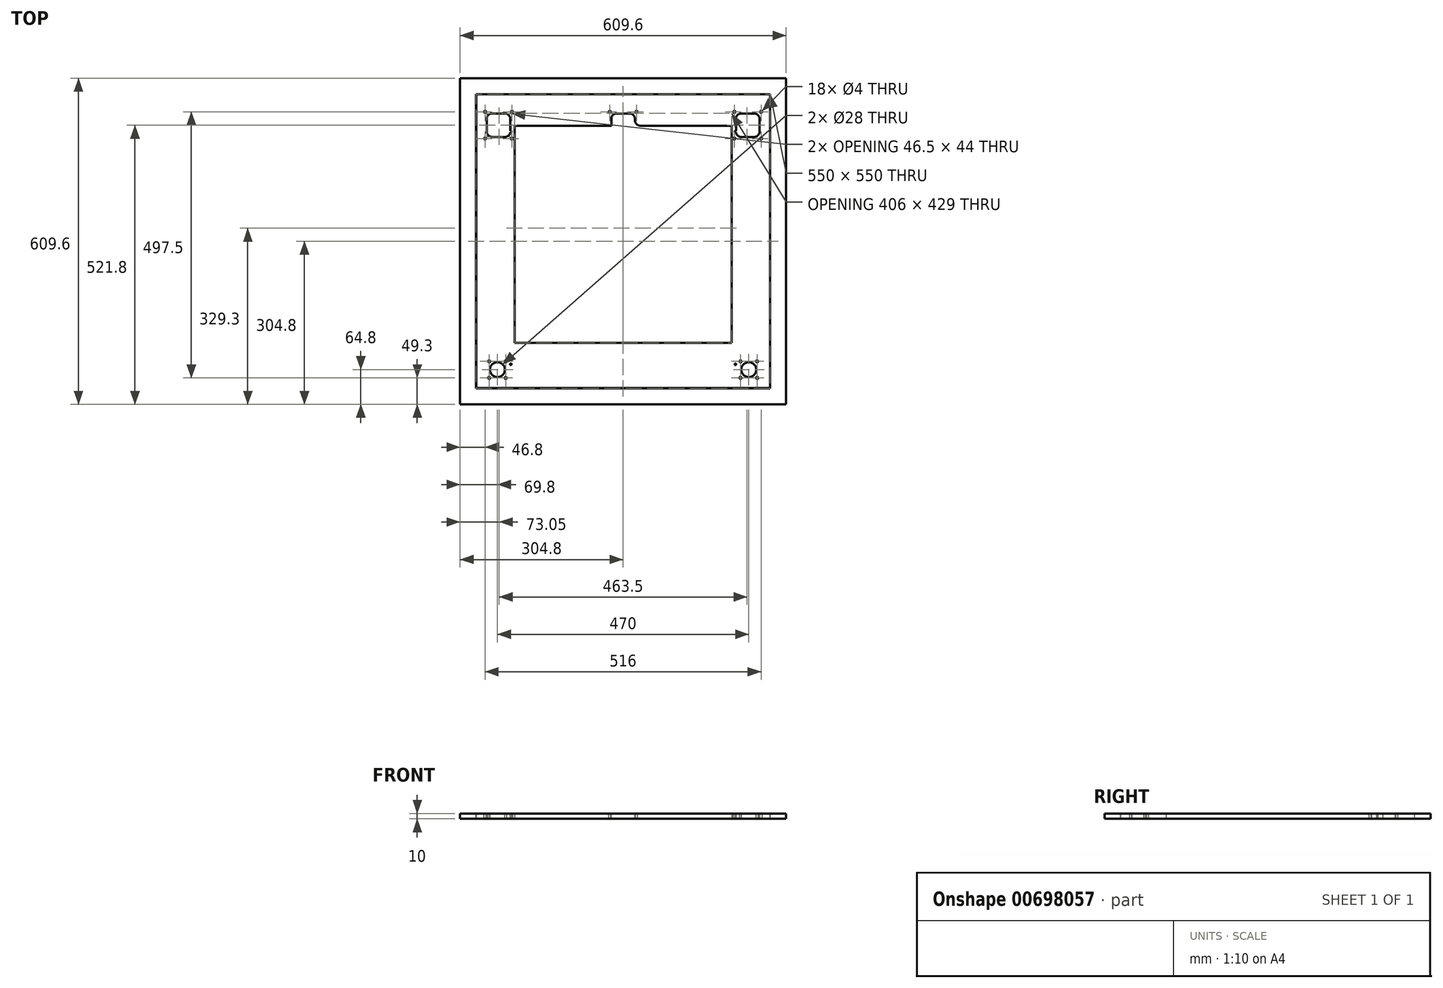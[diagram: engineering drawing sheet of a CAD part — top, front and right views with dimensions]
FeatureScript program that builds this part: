
annotation { "Feature Type Name" : "Feature", "Feature Type Description" : "" }
export const myFeature = defineFeature(function(context is Context, id is Id, definition is map)
    precondition{}
    {
        {
            var Q0;
            Q0=qCreatedBy(makeId("Top.planeOp"),FACE);
            var sketch = newSketch(context, id + "F0", { "sketchPlane" : qUnion([Q0])});
            skPoint(sketch, "E0.middle", {"position": v(0, 0) * mm});
            skLineSegment(sketch, "E1.bottom", {"start": v(-203, -190) * mm, "end": v(203, -190) * mm});
            skLineSegment(sketch, "E1.top", {"start": v(-203, 216) * mm, "end": v(203, 216) * mm});
            skLineSegment(sketch, "E1.left", {"start": v(-203, -190) * mm, "end": v(-203, 216) * mm});
            skLineSegment(sketch, "E1.right", {"start": v(203, -190) * mm, "end": v(203, 216) * mm});
            skLineSegment(sketch, "E2.bottom", {"start": v(274.64, -274.64) * mm, "end": v(-274.64, -274.64) * mm});
            skLineSegment(sketch, "E2.top", {"start": v(274.64, 274.64) * mm, "end": v(-274.64, 274.64) * mm});
            skLineSegment(sketch, "E2.left", {"start": v(274.64, -274.64) * mm, "end": v(274.64, 274.64) * mm});
            skLineSegment(sketch, "E2.right", {"start": v(-274.64, -274.64) * mm, "end": v(-274.64, 274.64) * mm});
            skLineSegment(sketch, "E3.bottom", {"start": v(-274.64, 274.64) * mm, "end": v(-223.84, 274.64) * mm});
            skLineSegment(sketch, "E3.top", {"start": v(-274.64, 223.84) * mm, "end": v(-223.84, 223.84) * mm});
            skLineSegment(sketch, "E3.left", {"start": v(-274.64, 274.64) * mm, "end": v(-274.64, 223.84) * mm});
            skLineSegment(sketch, "E3.right", {"start": v(-223.84, 274.64) * mm, "end": v(-223.84, 223.84) * mm});
            skLineSegment(sketch, "E4.bottom", {"start": v(274.64, 274.64) * mm, "end": v(223.84, 274.64) * mm});
            skLineSegment(sketch, "E4.top", {"start": v(274.64, 223.84) * mm, "end": v(223.84, 223.84) * mm});
            skLineSegment(sketch, "E4.left", {"start": v(274.64, 274.64) * mm, "end": v(274.64, 223.84) * mm});
            skLineSegment(sketch, "E4.right", {"start": v(223.84, 274.64) * mm, "end": v(223.84, 223.84) * mm});
            skLineSegment(sketch, "E5.bottom", {"start": v(-274.64, -274.64) * mm, "end": v(-223.84, -274.64) * mm});
            skLineSegment(sketch, "E5.top", {"start": v(-274.64, -223.84) * mm, "end": v(-223.84, -223.84) * mm});
            skLineSegment(sketch, "E5.left", {"start": v(-274.64, -274.64) * mm, "end": v(-274.64, -223.84) * mm});
            skLineSegment(sketch, "E5.right", {"start": v(-223.84, -274.64) * mm, "end": v(-223.84, -223.84) * mm});
            skLineSegment(sketch, "E6.bottom", {"start": v(274.64, -274.64) * mm, "end": v(223.84, -274.64) * mm});
            skLineSegment(sketch, "E6.top", {"start": v(274.64, -223.84) * mm, "end": v(223.84, -223.84) * mm});
            skLineSegment(sketch, "E6.left", {"start": v(274.64, -274.64) * mm, "end": v(274.64, -223.84) * mm});
            skLineSegment(sketch, "E6.right", {"start": v(223.84, -274.64) * mm, "end": v(223.84, -223.84) * mm});
            skSolve(sketch);
        }
        {
            var Q0;
            Q0 = qSketchRegion(id + "F0", true);
            var Q1;
            {var subQ5=sQuery(id+"F0.wireOp",EDGE,"E2.right");Q1=makeQuery(id+"F0.imprint","IMPRINT",FACE,{"disambiguationData":[TD([[makeQuery(id+"F0.imprint","IMPRINT",EDGE,{"derivedFrom":subQ5}),-1.0]])]});}
            var Q2;
            Q2=makeQuery(id+"F0.imprint","IMPRINT",FACE,{"disambiguationData":[TD([[makeQuery(id+"F0.imprint","IMPRINT",EDGE,{"derivedFrom":sQuery(id+"F0.wireOp",EDGE,"E1.bottom")}),-1.0]])]});
            var Q3;
            {var subQ0=sQuery(id+"F0.wireOp",EDGE,"E0.right");var subQ1=sQuery(id+"F0.wireOp",EDGE,"E0.top");var subQ2=makeQuery(id+"F0.imprint","INTERSECT",VERTEX,{"derivedFrom":[subQ1,subQ0]});Q3=makeQuery(id+"F0.imprint","IMPRINT",FACE,{"disambiguationData":[TD([[makeQuery(id+"F0.imprint","IMPRINT",EDGE,{"disambiguationData":[TD([[subQ2,1.0]])],"derivedFrom":subQ1}),1.0]])]});}
            var Q4;
            {var subQ0=sQuery(id+"F0.wireOp",EDGE,"E0.left");var subQ1=sQuery(id+"F0.wireOp",EDGE,"E0.top");var subQ2=makeQuery(id+"F0.imprint","INTERSECT",VERTEX,{"derivedFrom":[subQ1,subQ0]});Q4=makeQuery(id+"F0.imprint","IMPRINT",FACE,{"disambiguationData":[TD([[makeQuery(id+"F0.imprint","IMPRINT",EDGE,{"disambiguationData":[TD([[subQ2,-1.0]])],"derivedFrom":subQ1}),1.0]])]});}
            var Q5;
            {var subQ0=sQuery(id+"F0.wireOp",EDGE,"E0.left");var subQ1=sQuery(id+"F0.wireOp",EDGE,"E0.bottom");var subQ2=makeQuery(id+"F0.imprint","INTERSECT",VERTEX,{"derivedFrom":[subQ1,subQ0]});Q5=makeQuery(id+"F0.imprint","IMPRINT",FACE,{"disambiguationData":[TD([[makeQuery(id+"F0.imprint","IMPRINT",EDGE,{"disambiguationData":[TD([[subQ2,-1.0]])],"derivedFrom":subQ1}),-1.0]])]});}
            var Q6;
            {var subQ0=sQuery(id+"F0.wireOp",EDGE,"E0.right");var subQ1=sQuery(id+"F0.wireOp",EDGE,"E0.bottom");var subQ2=makeQuery(id+"F0.imprint","INTERSECT",VERTEX,{"derivedFrom":[subQ1,subQ0]});Q6=makeQuery(id+"F0.imprint","IMPRINT",FACE,{"disambiguationData":[TD([[makeQuery(id+"F0.imprint","IMPRINT",EDGE,{"disambiguationData":[TD([[subQ2,1.0]])],"derivedFrom":subQ1}),-1.0]])]});}
            extrude(context, id + "F1", {"entities" : qUnion([Q0, Q1, Q2, Q3, Q4, Q5, Q6]), "depth" : 10 * mm, "offsetDistance" : 25 * mm});
        }
        {
            var Q0;
            Q0=makeQuery(id+"F1.opExtrude","CAP_FACE",FACE,{"disambiguationData":[OSD([sQuery(id+"F0.wireOp",EDGE,"E0.bottom"),sQuery(id+"F0.wireOp",EDGE,"E0.top"),sQuery(id+"F0.wireOp",EDGE,"E0.left"),sQuery(id+"F0.wireOp",EDGE,"E0.right"),sQuery(id+"F0.wireOp",EDGE,"E1.bottom"),sQuery(id+"F0.wireOp",EDGE,"E1.top"),sQuery(id+"F0.wireOp",EDGE,"E1.left"),sQuery(id+"F0.wireOp",EDGE,"E1.right")])],"isStart":true});
            var sketch = newSketch(context, id + "F2", { "sketchPlane" : qUnion([Q0])});
            skLineSegment(sketch, "E7.bottom", {"start": v(-210, 230) * mm, "end": v(210, 230) * mm});
            skLineSegment(sketch, "E7.top", {"start": v(-210, -205) * mm, "end": v(210, -205) * mm});
            skLineSegment(sketch, "E7.left", {"start": v(-210, 230) * mm, "end": v(-210, -205) * mm});
            skLineSegment(sketch, "E7.right", {"start": v(210, 230) * mm, "end": v(210, -205) * mm});
            skPoint(sketch, "E7.middle", {"position": v(0, 0) * mm});
            skLineSegment(sketch, "E8", {"start": v(0, 0) * mm, "end": v(210, 0) * mm, "construction": true});
            skLineSegment(sketch, "E9", {"start": v(0, 0) * mm, "end": v(-210, 0) * mm, "construction": true});
            skSolve(sketch);
        }
        {
            var Q0;
            Q0=makeQuery(id+"F1.opExtrude","CAP_FACE",FACE,{"disambiguationData":[OSD([sQuery(id+"F0.wireOp",EDGE,"E0.bottom"),sQuery(id+"F0.wireOp",EDGE,"E0.top"),sQuery(id+"F0.wireOp",EDGE,"E0.left"),sQuery(id+"F0.wireOp",EDGE,"E0.right"),sQuery(id+"F0.wireOp",EDGE,"E1.bottom"),sQuery(id+"F0.wireOp",EDGE,"E1.top"),sQuery(id+"F0.wireOp",EDGE,"E1.left"),sQuery(id+"F0.wireOp",EDGE,"E1.right")])],"isStart":false});
            var sketch = newSketch(context, id + "F3", { "sketchPlane" : qUnion([Q0])});
            skLineSegment(sketch, "E10", {"start": v(0, 0) * mm, "end": v(0, 275) * mm, "construction": true});
            skLineSegment(sketch, "E11", {"start": v(0, 275) * mm, "end": v(0, 275) * mm});
            skLineSegment(sketch, "E12", {"start": v(0, 217) * mm, "end": v(233, 217) * mm, "construction": true});
            skLineSegment(sketch, "E13.bottom", {"start": v(255, 195) * mm, "end": v(211, 195) * mm});
            skLineSegment(sketch, "E13.top", {"start": v(255, 239) * mm, "end": v(211, 239) * mm});
            skLineSegment(sketch, "E13.left", {"start": v(255, 195) * mm, "end": v(255, 239) * mm});
            skLineSegment(sketch, "E13.right", {"start": v(211, 195) * mm, "end": v(211, 239) * mm});
            skPoint(sketch, "E13.middle", {"position": v(233, 217) * mm});
            skLineSegment(sketch, "E14.MirrorCS", {"start": v(0, 217) * mm, "end": v(-233, 217) * mm, "construction": true});
            skLineSegment(sketch, "E15.MirrorCS", {"start": v(-255, 239) * mm, "end": v(-211, 239) * mm});
            skLineSegment(sketch, "E16.MirrorCS", {"start": v(-255, 195) * mm, "end": v(-211, 195) * mm});
            skPoint(sketch, "E17.MirrorP", {"position": v(-233, 217) * mm});
            skLineSegment(sketch, "E18.MirrorCS", {"start": v(-255, 195) * mm, "end": v(-255, 239) * mm});
            skLineSegment(sketch, "E19.MirrorCS", {"start": v(-211, 195) * mm, "end": v(-211, 239) * mm});
            skLineSegment(sketch, "E20.bottom", {"start": v(258, 192) * mm, "end": v(208, 192) * mm});
            skLineSegment(sketch, "E20.top", {"start": v(258, 242) * mm, "end": v(208, 242) * mm});
            skLineSegment(sketch, "E20.left", {"start": v(258, 192) * mm, "end": v(258, 242) * mm});
            skLineSegment(sketch, "E20.right", {"start": v(208, 192) * mm, "end": v(208, 242) * mm});
            skLineSegment(sketch, "E21.bottom", {"start": v(-208, 192) * mm, "end": v(-258, 192) * mm});
            skLineSegment(sketch, "E21.top", {"start": v(-208, 242) * mm, "end": v(-258, 242) * mm});
            skLineSegment(sketch, "E21.left", {"start": v(-208, 192) * mm, "end": v(-208, 242) * mm});
            skLineSegment(sketch, "E21.right", {"start": v(-258, 192) * mm, "end": v(-258, 242) * mm});
            skLineSegment(sketch, "E22.bottom", {"start": v(-22, 239) * mm, "end": v(22, 239) * mm});
            skLineSegment(sketch, "E22.top", {"start": v(-22, 195) * mm, "end": v(22, 195) * mm});
            skLineSegment(sketch, "E22.left", {"start": v(-22, 239) * mm, "end": v(-22, 195) * mm});
            skLineSegment(sketch, "E22.right", {"start": v(22, 239) * mm, "end": v(22, 195) * mm});
            skPoint(sketch, "E22.middle", {"position": v(0, 217) * mm});
            skLineSegment(sketch, "E23.bottom", {"start": v(-25, 242) * mm, "end": v(25, 242) * mm});
            skLineSegment(sketch, "E23.top", {"start": v(-25, 192) * mm, "end": v(25, 192) * mm});
            skLineSegment(sketch, "E23.left", {"start": v(-25, 242) * mm, "end": v(-25, 192) * mm});
            skLineSegment(sketch, "E23.right", {"start": v(25, 242) * mm, "end": v(25, 192) * mm});
            skLineSegment(sketch, "E24", {"start": v(0, 0) * mm, "end": v(0, -240) * mm, "construction": true});
            skLineSegment(sketch, "E25", {"start": v(0, -240) * mm, "end": v(-235, -240) * mm, "construction": true});
            skLineSegment(sketch, "E26.bottom", {"start": v(15.5, -255.5) * mm, "end": v(-15.5, -255.5) * mm});
            skLineSegment(sketch, "E26.top", {"start": v(15.5, -224.5) * mm, "end": v(-15.5, -224.5) * mm});
            skLineSegment(sketch, "E26.left", {"start": v(15.5, -255.5) * mm, "end": v(15.5, -224.5) * mm});
            skLineSegment(sketch, "E26.right", {"start": v(-15.5, -255.5) * mm, "end": v(-15.5, -224.5) * mm});
            skPoint(sketch, "E26.middle", {"position": v(0, -240) * mm});
            skLineSegment(sketch, "E27.bottom", {"start": v(-219.5, -255.5) * mm, "end": v(-250.5, -255.5) * mm});
            skLineSegment(sketch, "E27.top", {"start": v(-219.5, -224.5) * mm, "end": v(-250.5, -224.5) * mm});
            skLineSegment(sketch, "E27.left", {"start": v(-219.5, -255.5) * mm, "end": v(-219.5, -224.5) * mm});
            skLineSegment(sketch, "E27.right", {"start": v(-250.5, -255.5) * mm, "end": v(-250.5, -224.5) * mm});
            skPoint(sketch, "E27.middle", {"position": v(-235, -240) * mm});
            skLineSegment(sketch, "E28.MirrorCS", {"start": v(0, -240) * mm, "end": v(235, -240) * mm, "construction": true});
            skLineSegment(sketch, "E29.MirrorCS", {"start": v(219.5, -255.5) * mm, "end": v(219.5, -224.5) * mm});
            skLineSegment(sketch, "E30.MirrorCS", {"start": v(250.5, -255.5) * mm, "end": v(250.5, -224.5) * mm});
            skPoint(sketch, "E31.MirrorP", {"position": v(235, -240) * mm});
            skLineSegment(sketch, "E32.MirrorCS", {"start": v(219.5, -255.5) * mm, "end": v(250.5, -255.5) * mm});
            skLineSegment(sketch, "E33.MirrorCS", {"start": v(219.5, -224.5) * mm, "end": v(250.5, -224.5) * mm});
            skCircle(sketch, "E34", {"center": v(-235, -240) * mm, "radius": 14 * mm});
            skCircle(sketch, "E35", {"center": v(0, -240) * mm, "radius": 14 * mm});
            skCircle(sketch, "E36", {"center": v(235, -240) * mm, "radius": 14 * mm});
            skSolve(sketch);
        }
        {
            var Q0;
            Q0=makeQuery(id+"F3.imprint","IMPRINT",FACE,{"disambiguationData":[TD([[makeQuery(id+"F3.imprint","IMPRINT",EDGE,{"derivedFrom":sQuery(id+"F3.wireOp",EDGE,"E15.MirrorCS")}),-1.0]])]});
            var Q1;
            Q1=makeQuery(id+"F3.imprint","IMPRINT",FACE,{"disambiguationData":[TD([[makeQuery(id+"F3.imprint","IMPRINT",EDGE,{"derivedFrom":sQuery(id+"F3.wireOp",EDGE,"E13.bottom")}),-1.0]])]});
            var Q2;
            Q2=makeQuery(id+"F3.imprint","IMPRINT",FACE,{"disambiguationData":[TD([[makeQuery(id+"F3.imprint","IMPRINT",EDGE,{"derivedFrom":sQuery(id+"F3.wireOp",EDGE,"E22.bottom")}),-1.0]])]});
            var Q3;
            Q3=makeQuery(id+"F3.imprint","IMPRINT",FACE,{"disambiguationData":[TD([[makeQuery(id+"F3.imprint","IMPRINT",EDGE,{"derivedFrom":sQuery(id+"F3.wireOp",EDGE,"E34")}),1.0]])]});
            var Q4;
            Q4=makeQuery(id+"F3.imprint","IMPRINT",FACE,{"disambiguationData":[TD([[makeQuery(id+"F3.imprint","IMPRINT",EDGE,{"derivedFrom":sQuery(id+"F3.wireOp",EDGE,"E36")}),1.0]])]});
            extrude(context, id + "F4", {"entities" : qUnion([Q0, Q1, Q2, Q3, Q4]), "operationType" : NewBodyOperationType.REMOVE, "oppositeDirection" : true, "depth" : 25 * mm, "offsetDistance" : 25 * mm});
        }
        {
            var Q0;
            Q0=makeQuery(id+"F3.imprint","IMPRINT",FACE,{"disambiguationData":[TD([[makeQuery(id+"F3.imprint","IMPRINT",EDGE,{"derivedFrom":makeQuery(id+"F1.opExtrude","CAP_EDGE",EDGE,{"disambiguationData":[OSD([sQuery(id+"F0.wireOp",EDGE,"E1.bottom")])],"isStart":false})}),1.0]])]});
            var sketch = newSketch(context, id + "F5", { "sketchPlane" : qUnion([Q0])});
            skLineSegment(sketch, "E37.bottom", {"start": v(304.8, -304.8) * mm, "end": v(-304.8, -304.8) * mm});
            skLineSegment(sketch, "E37.top", {"start": v(304.8, 304.8) * mm, "end": v(-304.8, 304.8) * mm});
            skLineSegment(sketch, "E37.left", {"start": v(304.8, -304.8) * mm, "end": v(304.8, 304.8) * mm});
            skLineSegment(sketch, "E37.right", {"start": v(-304.8, -304.8) * mm, "end": v(-304.8, 304.8) * mm});
            skPoint(sketch, "E37.middle", {"position": v(0, 0) * mm});
            skLineSegment(sketch, "E38.bottom", {"start": v(275, -275) * mm, "end": v(-275, -275) * mm});
            skLineSegment(sketch, "E38.top", {"start": v(275, 275) * mm, "end": v(-275, 275) * mm});
            skLineSegment(sketch, "E38.left", {"start": v(275, -275) * mm, "end": v(275, 275) * mm});
            skLineSegment(sketch, "E38.right", {"start": v(-275, -275) * mm, "end": v(-275, 275) * mm});
            skSolve(sketch);
        }
        {
            var Q0;
            Q0=makeQuery(id+"F5.imprint","IMPRINT",FACE,{"disambiguationData":[TD([[makeQuery(id+"F5.imprint","IMPRINT",EDGE,{"derivedFrom":sQuery(id+"F5.wireOp",EDGE,"E37.bottom")}),-1.0]])]});
            extrude(context, id + "F6", {"entities" : qUnion([Q0]), "oppositeDirection" : true, "depth" : 10 * mm, "offsetDistance" : 25 * mm});
        }
        {
            var Q0;
            Q0=makeQuery(id+"F4.boolean.opBoolean","COPY",EDGE,{"derivedFrom":makeQuery(id+"F4.opExtrude","SWEPT_EDGE",EDGE,{"disambiguationData":[OSD([sQuery(id+"F3.wireOp",EDGE,"E13.bottom"),sQuery(id+"F3.wireOp",EDGE,"E13.left")])]})});
            var Q1;
            Q1=makeQuery(id+"F4.boolean.opBoolean","COPY",EDGE,{"derivedFrom":makeQuery(id+"F4.opExtrude","SWEPT_EDGE",EDGE,{"disambiguationData":[OSD([sQuery(id+"F3.wireOp",EDGE,"E13.top"),sQuery(id+"F3.wireOp",EDGE,"E13.left")])]})});
            var Q2;
            Q2=makeQuery(id+"F4.boolean.opBoolean","COPY",EDGE,{"derivedFrom":makeQuery(id+"F4.opExtrude","SWEPT_EDGE",EDGE,{"disambiguationData":[OSD([sQuery(id+"F3.wireOp",EDGE,"E22.top"),sQuery(id+"F3.wireOp",EDGE,"E22.right")])]})});
            var Q3;
            Q3=makeQuery(id+"F4.boolean.opBoolean","COPY",EDGE,{"derivedFrom":makeQuery(id+"F4.opExtrude","SWEPT_EDGE",EDGE,{"disambiguationData":[OSD([sQuery(id+"F3.wireOp",EDGE,"E22.bottom"),sQuery(id+"F3.wireOp",EDGE,"E22.left")])]})});
            var Q4;
            Q4=makeQuery(id+"F4.boolean.opBoolean","COPY",EDGE,{"derivedFrom":makeQuery(id+"F4.opExtrude","SWEPT_EDGE",EDGE,{"disambiguationData":[OSD([sQuery(id+"F3.wireOp",EDGE,"E22.bottom"),sQuery(id+"F3.wireOp",EDGE,"E22.right")])]})});
            var Q5;
            Q5=makeQuery(id+"F4.boolean.opBoolean","COPY",EDGE,{"derivedFrom":makeQuery(id+"F4.opExtrude","SWEPT_EDGE",EDGE,{"disambiguationData":[OSD([sQuery(id+"F3.wireOp",EDGE,"E22.top"),sQuery(id+"F3.wireOp",EDGE,"E22.left")])]})});
            var Q6;
            Q6=makeQuery(id+"F4.boolean.opBoolean","COPY",EDGE,{"derivedFrom":makeQuery(id+"F4.opExtrude","SWEPT_EDGE",EDGE,{"disambiguationData":[OSD([sQuery(id+"F3.wireOp",EDGE,"E16.MirrorCS"),sQuery(id+"F3.wireOp",EDGE,"E18.MirrorCS")])]})});
            var Q7;
            Q7=makeQuery(id+"F4.boolean.opBoolean","COPY",EDGE,{"derivedFrom":makeQuery(id+"F4.opExtrude","SWEPT_EDGE",EDGE,{"disambiguationData":[OSD([sQuery(id+"F3.wireOp",EDGE,"E16.MirrorCS"),sQuery(id+"F3.wireOp",EDGE,"E19.MirrorCS")])]})});
            var Q8;
            Q8=makeQuery(id+"F4.boolean.opBoolean","COPY",EDGE,{"derivedFrom":makeQuery(id+"F4.opExtrude","SWEPT_EDGE",EDGE,{"disambiguationData":[OSD([sQuery(id+"F3.wireOp",EDGE,"E15.MirrorCS"),sQuery(id+"F3.wireOp",EDGE,"E18.MirrorCS")])]})});
            var Q9;
            Q9=makeQuery(id+"F4.boolean.opBoolean","COPY",EDGE,{"derivedFrom":makeQuery(id+"F4.opExtrude","SWEPT_EDGE",EDGE,{"disambiguationData":[OSD([sQuery(id+"F3.wireOp",EDGE,"E15.MirrorCS"),sQuery(id+"F3.wireOp",EDGE,"E19.MirrorCS")])]})});
            var Q10;
            Q10=makeQuery(id+"F4.boolean.opBoolean","COPY",EDGE,{"derivedFrom":makeQuery(id+"F4.opExtrude","SWEPT_EDGE",EDGE,{"disambiguationData":[OSD([sQuery(id+"F3.wireOp",EDGE,"E13.bottom"),sQuery(id+"F3.wireOp",EDGE,"E13.right")])]})});
            var Q11;
            Q11=makeQuery(id+"F4.boolean.opBoolean","COPY",EDGE,{"derivedFrom":makeQuery(id+"F4.opExtrude","SWEPT_EDGE",EDGE,{"disambiguationData":[OSD([sQuery(id+"F3.wireOp",EDGE,"E13.top"),sQuery(id+"F3.wireOp",EDGE,"E13.right")])]})});
            fillet(context, id + "F7", {"entities" : qUnion([Q0, Q1, Q2, Q3, Q4, Q5, Q6, Q7, Q8, Q9, Q10, Q11]), "radius" : 10 * mm, "tangentPropagation" : true, "allowEdgeOverflow" : false});
        }
        {
            var Q0;
            Q0=sQuery(id+"F3.wireOp",VERTEX,"E21.bottom.end");
            var Q1;
            Q1=sQuery(id+"F3.wireOp",VERTEX,"E21.top.end");
            var Q2;
            Q2=sQuery(id+"F3.wireOp",VERTEX,"E21.left.end");
            var Q3;
            Q3=sQuery(id+"F3.wireOp",VERTEX,"E21.left.start");
            var Q4;
            Q4=sQuery(id+"F3.wireOp",VERTEX,"E23.right.end");
            var Q5;
            Q5=sQuery(id+"F3.wireOp",VERTEX,"E23.bottom.end");
            var Q6;
            Q6=sQuery(id+"F3.wireOp",VERTEX,"E23.bottom.start");
            var Q7;
            Q7=sQuery(id+"F3.wireOp",VERTEX,"E20.right.start");
            var Q8;
            Q8=sQuery(id+"F3.wireOp",VERTEX,"E20.left.end");
            var Q9;
            Q9=sQuery(id+"F3.wireOp",VERTEX,"E20.top.end");
            var Q10;
            Q10=sQuery(id+"F3.wireOp",VERTEX,"E23.top.start");
            var Q11;
            Q11=sQuery(id+"F3.wireOp",VERTEX,"E20.bottom.start");
            var Q12;
            Q12=sQuery(id+"F3.wireOp",VERTEX,"E27.right.start");
            var Q13;
            Q13=sQuery(id+"F3.wireOp",VERTEX,"E27.top.end");
            var Q14;
            Q14=sQuery(id+"F3.wireOp",VERTEX,"E27.left.end");
            var Q15;
            Q15=sQuery(id+"F3.wireOp",VERTEX,"E27.left.start");
            var Q16;
            Q16=sQuery(id+"F3.wireOp",VERTEX,"E30.MirrorCS.start");
            var Q17;
            Q17=sQuery(id+"F3.wireOp",VERTEX,"E29.MirrorCS.end");
            var Q18;
            Q18=sQuery(id+"F3.wireOp",VERTEX,"E29.MirrorCS.start");
            var Q19;
            Q19=sQuery(id+"F3.wireOp",VERTEX,"E33.MirrorCS.end");
            var Q20;
            Q20=makeQuery(id+"F1.opExtrude","SWEPT_BODY",BODY,{"disambiguationData":[OSD([sQuery(id+"F0.wireOp",EDGE,"E1.bottom"),sQuery(id+"F0.wireOp",EDGE,"E1.top"),sQuery(id+"F0.wireOp",EDGE,"E1.left"),sQuery(id+"F0.wireOp",EDGE,"E1.right"),sQuery(id+"F0.wireOp",EDGE,"E2.bottom"),sQuery(id+"F0.wireOp",EDGE,"E2.top"),sQuery(id+"F0.wireOp",EDGE,"E2.left"),sQuery(id+"F0.wireOp",EDGE,"E2.right"),sQuery(id+"F0.wireOp",EDGE,"E3.bottom"),sQuery(id+"F0.wireOp",EDGE,"E3.left"),sQuery(id+"F0.wireOp",EDGE,"E4.bottom"),sQuery(id+"F0.wireOp",EDGE,"E4.left"),sQuery(id+"F0.wireOp",EDGE,"E5.bottom"),sQuery(id+"F0.wireOp",EDGE,"E5.left"),sQuery(id+"F0.wireOp",EDGE,"E6.bottom"),sQuery(id+"F0.wireOp",EDGE,"E6.left")])]});
            hole(context, id + "F8", {"style" : HoleStyle.SIMPLE, "endStyle" : HoleEndStyle.THROUGH, "holeDiameter" : 4 * mm, "majorDiameter" : 5 * mm, "isTappedThrough" : true, "tappedDepth" : 12 * mm, "tapClearance" : 3, "locations" : qUnion([Q0, Q1, Q2, Q3, Q4, Q5, Q6, Q7, Q8, Q9, Q10, Q11, Q12, Q13, Q14, Q15, Q16, Q17, Q18, Q19]), "scope" : qUnion([Q20])});
        }
        {
            var Q0;
            Q0=sQuery(id+"F2.wireOp",VERTEX,"E7.top.start");
            var Q1;
            Q1=sQuery(id+"F2.wireOp",VERTEX,"E7.right.end");
            var Q2;
            Q2=sQuery(id+"F2.wireOp",VERTEX,"E7.right.start");
            var Q3;
            Q3=sQuery(id+"F2.wireOp",VERTEX,"E7.bottom.start");
            var Q4;
            Q4=makeQuery(id+"F1.opExtrude","SWEPT_BODY",BODY,{"disambiguationData":[OSD([sQuery(id+"F0.wireOp",EDGE,"E1.bottom"),sQuery(id+"F0.wireOp",EDGE,"E1.top"),sQuery(id+"F0.wireOp",EDGE,"E1.left"),sQuery(id+"F0.wireOp",EDGE,"E1.right"),sQuery(id+"F0.wireOp",EDGE,"E2.bottom"),sQuery(id+"F0.wireOp",EDGE,"E2.top"),sQuery(id+"F0.wireOp",EDGE,"E2.left"),sQuery(id+"F0.wireOp",EDGE,"E2.right"),sQuery(id+"F0.wireOp",EDGE,"E3.bottom"),sQuery(id+"F0.wireOp",EDGE,"E3.left"),sQuery(id+"F0.wireOp",EDGE,"E4.bottom"),sQuery(id+"F0.wireOp",EDGE,"E4.left"),sQuery(id+"F0.wireOp",EDGE,"E5.bottom"),sQuery(id+"F0.wireOp",EDGE,"E5.left"),sQuery(id+"F0.wireOp",EDGE,"E6.bottom"),sQuery(id+"F0.wireOp",EDGE,"E6.left")])]});
            hole(context, id + "F9", {"style" : HoleStyle.SIMPLE, "endStyle" : HoleEndStyle.THROUGH, "holeDiameter" : 3 * mm, "majorDiameter" : 5 * mm, "isTappedThrough" : true, "tappedDepth" : 12 * mm, "tapClearance" : 3, "locations" : qUnion([Q0, Q1, Q2, Q3]), "scope" : qUnion([Q4])});
        }
    });
